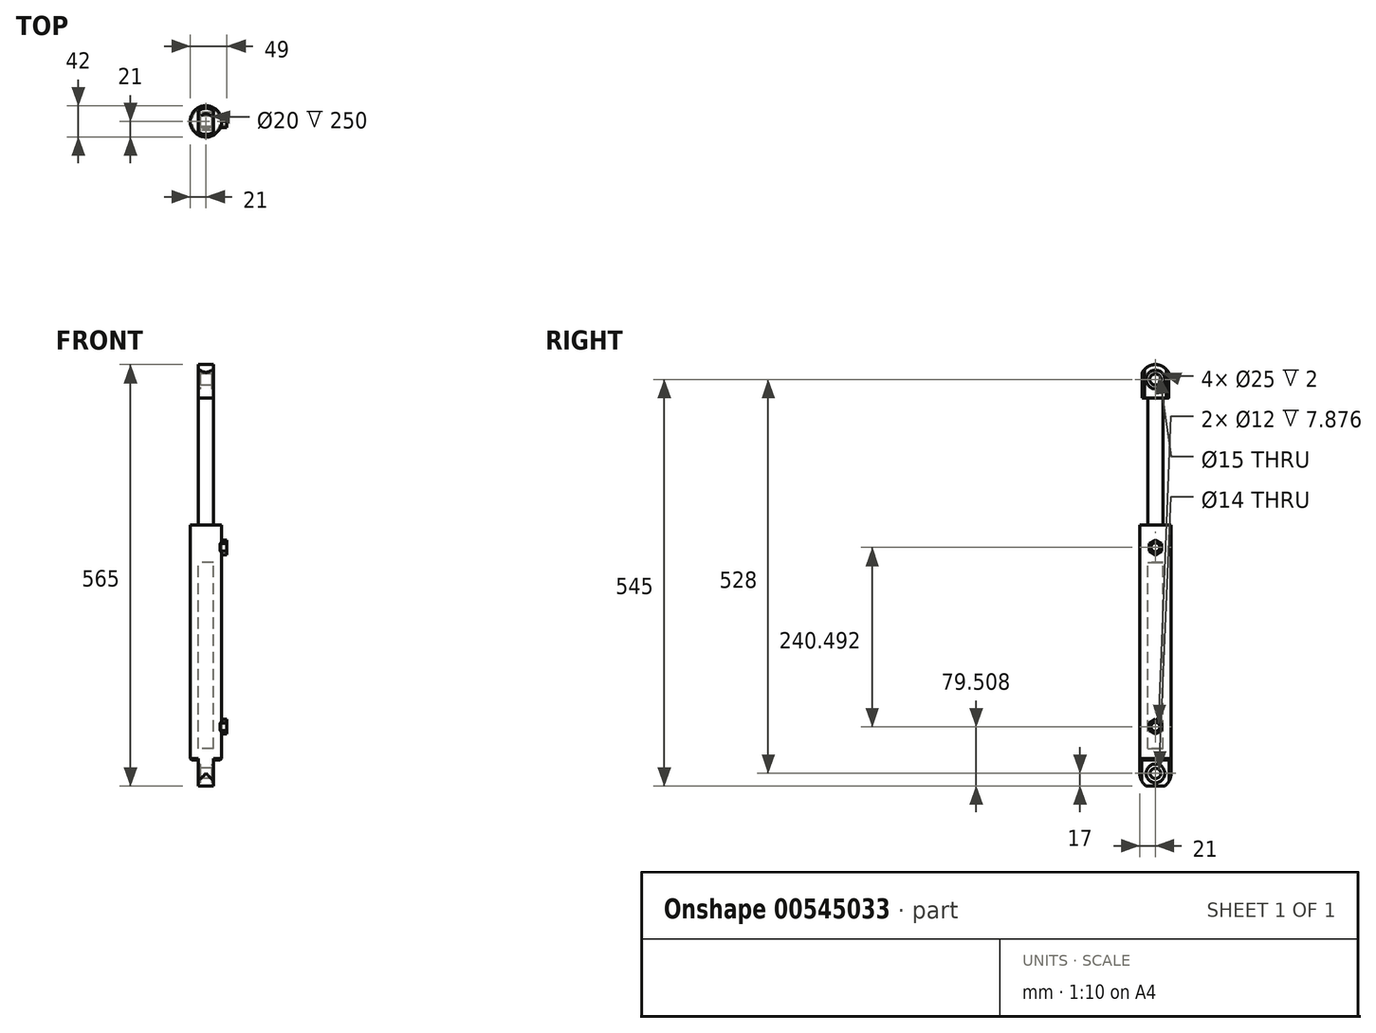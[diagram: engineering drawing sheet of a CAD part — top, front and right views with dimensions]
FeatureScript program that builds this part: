
annotation { "Feature Type Name" : "Feature", "Feature Type Description" : "" }
export const myFeature = defineFeature(function(context is Context, id is Id, definition is map)
    precondition{}
    {
        {
            var Q0;
            Q0=qCreatedBy(makeId("Top.planeOp"),FACE);
            var sketch = newSketch(context, id + "F0", { "sketchPlane" : qUnion([Q0])});
            skCircle(sketch, "E0", {"center": v(0, 0) * mm, "radius": 21 * mm});
            skSolve(sketch);
        }
        {
            var Q0;
            Q0 = qSketchRegion(id + "F0", true);
            extrude(context, id + "F1", {"entities" : qUnion([Q0]), "depth" : 315 * mm, "offsetDistance" : 25 * mm});
        }
        {
            var Q0;
            Q0=makeQuery(id+"F1.opExtrude","CAP_FACE",FACE,{"disambiguationData":[OSD([sQuery(id+"F0.wireOp",EDGE,"E0")])],"isStart":false});
            var sketch = newSketch(context, id + "F2", { "sketchPlane" : qUnion([Q0])});
            skCircle(sketch, "E1", {"center": v(0, 0) * mm, "radius": 10 * mm});
            skSolve(sketch);
        }
        {
            var Q0;
            Q0=makeQuery(id+"F2.imprint","IMPRINT",FACE,{"disambiguationData":[TD([[makeQuery(id+"F2.imprint","IMPRINT",EDGE,{"derivedFrom":sQuery(id+"F2.wireOp",EDGE,"E1")}),1.0]])]});
            extrude(context, id + "F3", {"entities" : qUnion([Q0]), "operationType" : NewBodyOperationType.REMOVE, "oppositeDirection" : true, "depth" : 300 * mm, "offsetDistance" : 25 * mm});
        }
        {
            var Q0;
            Q0=makeQuery(id+"F0.imprint","IMPRINT",FACE,{"disambiguationData":[TD([[makeQuery(id+"F0.imprint","IMPRINT",EDGE,{"derivedFrom":sQuery(id+"F0.wireOp",EDGE,"E0")}),1.0]])]});
            var sketch = newSketch(context, id + "F4", { "sketchPlane" : qUnion([Q0])});
            skCircle(sketch, "E2", {"center": v(0, 0) * mm, "radius": 21 * mm});
            skSolve(sketch);
        }
        {
            var Q0;
            Q0 = qSketchRegion(id + "F4", true);
            extrude(context, id + "F5", {"entities" : qUnion([Q0]), "operationType" : NewBodyOperationType.ADD, "oppositeDirection" : true, "depth" : 35 * mm, "offsetDistance" : 25 * mm});
        }
        {
            var Q0;
            Q0=makeQuery(id+"F5.opExtrude","CAP_FACE",FACE,{"disambiguationData":[OSD([sQuery(id+"F4.wireOp",EDGE,"E2")])],"isStart":false});
            var sketch = newSketch(context, id + "F6", { "sketchPlane" : qUnion([Q0])});
            skLineSegment(sketch, "E3", {"start": v(0, 0) * mm, "end": v(0, 21) * mm});
            skLineSegment(sketch, "E4.bottom", {"start": v(10, 24.47) * mm, "end": v(25.68, 24.47) * mm});
            skLineSegment(sketch, "E4.top", {"start": v(10, -25.36) * mm, "end": v(25.68, -25.36) * mm});
            skLineSegment(sketch, "E4.left", {"start": v(10, 24.47) * mm, "end": v(10, -25.36) * mm});
            skLineSegment(sketch, "E4.right", {"start": v(25.68, 24.47) * mm, "end": v(25.68, -25.36) * mm});
            skLineSegment(sketch, "E5.bottom", {"start": v(-10, 23.89) * mm, "end": v(-26.25, 23.89) * mm});
            skLineSegment(sketch, "E5.top", {"start": v(-10, -20.96) * mm, "end": v(-26.25, -20.96) * mm});
            skLineSegment(sketch, "E5.left", {"start": v(-10, 23.89) * mm, "end": v(-10, -20.96) * mm});
            skLineSegment(sketch, "E5.right", {"start": v(-26.25, 23.89) * mm, "end": v(-26.25, -20.96) * mm});
            skSolve(sketch);
        }
        {
            var Q0;
            Q0 = qSketchRegion(id + "F6", true);
            extrude(context, id + "F7", {"entities" : qUnion([Q0]), "operationType" : NewBodyOperationType.REMOVE, "oppositeDirection" : true, "depth" : 35 * mm, "offsetDistance" : 25 * mm});
        }
        {
            var Q0;
            Q0=makeQuery(id+"F7.boolean.opBoolean","COPY",FACE,{"derivedFrom":makeQuery(id+"F7.opExtrude","SWEPT_FACE",FACE,{"disambiguationData":[OSD([sQuery(id+"F6.wireOp",EDGE,"E5.left")])]})});
            var sketch = newSketch(context, id + "F8", { "sketchPlane" : qUnion([Q0])});
            skCircle(sketch, "E6", {"center": v(0, -18) * mm, "radius": 12.5 * mm});
            skSolve(sketch);
        }
        {
            var Q0;
            Q0 = qSketchRegion(id + "F8", true);
            extrude(context, id + "F9", {"entities" : qUnion([Q0]), "operationType" : NewBodyOperationType.REMOVE, "oppositeDirection" : true, "depth" : 2 * mm, "offsetDistance" : 25 * mm});
        }
        {
            var Q0;
            Q0=makeQuery(id+"F9.boolean.opBoolean","COPY",FACE,{"derivedFrom":makeQuery(id+"F9.opExtrude","CAP_FACE",FACE,{"disambiguationData":[OSD([sQuery(id+"F8.wireOp",EDGE,"E6")])],"isStart":false})});
            var sketch = newSketch(context, id + "F10", { "sketchPlane" : qUnion([Q0])});
            skCircle(sketch, "E7", {"center": v(0, -18) * mm, "radius": 7 * mm});
            skSolve(sketch);
        }
        {
            var Q0;
            Q0 = qSketchRegion(id + "F10", true);
            extrude(context, id + "F11", {"entities" : qUnion([Q0]), "operationType" : NewBodyOperationType.REMOVE, "oppositeDirection" : true, "depth" : 25 * mm, "offsetDistance" : 25 * mm});
        }
        {
            var Q0;
            Q0=makeQuery(id+"F7.boolean.opBoolean","COPY",FACE,{"derivedFrom":makeQuery(id+"F7.opExtrude","SWEPT_FACE",FACE,{"disambiguationData":[OSD([sQuery(id+"F6.wireOp",EDGE,"E4.left")])]})});
            var sketch = newSketch(context, id + "F12", { "sketchPlane" : qUnion([Q0])});
            skCircle(sketch, "E8", {"center": v(0, -18) * mm, "radius": 12.5 * mm});
            skSolve(sketch);
        }
        {
            var Q0;
            Q0 = qSketchRegion(id + "F12", true);
            extrude(context, id + "F13", {"entities" : qUnion([Q0]), "operationType" : NewBodyOperationType.REMOVE, "oppositeDirection" : true, "depth" : 2 * mm, "offsetDistance" : 25 * mm});
        }
        {
            var Q0;
            Q0=makeQuery(id+"F7.boolean.opBoolean","COPY",FACE,{"derivedFrom":makeQuery(id+"F7.opExtrude","SWEPT_FACE",FACE,{"disambiguationData":[OSD([sQuery(id+"F6.wireOp",EDGE,"E5.left")])]})});
            var sketch = newSketch(context, id + "F14", { "sketchPlane" : qUnion([Q0])});
            skArc(sketch, "E9", {"start": v(-21, -18) * mm, "mid": v(0, -39) * mm, "end": v(21, -18) * mm});
            skArc(sketch, "E10", {"start": v(-30, -18) * mm, "mid": v(0, -48) * mm, "end": v(30, -18) * mm});
            skLineSegment(sketch, "E11", {"start": v(30, -18) * mm, "end": v(21, -18) * mm});
            skLineSegment(sketch, "E12.trimOffspring", {"start": v(-21, -18) * mm, "end": v(-30, -18) * mm});
            skSolve(sketch);
        }
        {
            var Q0;
            Q0 = qSketchRegion(id + "F14", true);
            extrude(context, id + "F15", {"entities" : qUnion([Q0]), "operationType" : NewBodyOperationType.REMOVE, "oppositeDirection" : true, "depth" : 25 * mm, "offsetDistance" : 25 * mm});
        }
        {
            var Q0;
            Q0=makeQuery(id+"F7.boolean.opBoolean","INTERSECT",EDGE,{"derivedFrom":[makeQuery(id+"F5.boolean.opBoolean","MERGE",FACE,{"derivedFrom":[makeQuery(id+"F1.opExtrude","SWEPT_FACE",FACE,{"disambiguationData":[OSD([sQuery(id+"F0.wireOp",EDGE,"E0")])]}),makeQuery(id+"F5.opExtrude","SWEPT_FACE",FACE,{"disambiguationData":[OSD([sQuery(id+"F4.wireOp",EDGE,"E2")])]})]}),makeQuery(id+"F7.opExtrude","CAP_FACE",FACE,{"disambiguationData":[OSD([sQuery(id+"F6.wireOp",EDGE,"E4.bottom"),sQuery(id+"F6.wireOp",EDGE,"E4.top"),sQuery(id+"F6.wireOp",EDGE,"E4.left"),sQuery(id+"F6.wireOp",EDGE,"E4.right")])],"isStart":false})]});
            var Q1;
            Q1=makeQuery(id+"F7.boolean.opBoolean","INTERSECT",EDGE,{"derivedFrom":[makeQuery(id+"F5.boolean.opBoolean","MERGE",FACE,{"derivedFrom":[makeQuery(id+"F1.opExtrude","SWEPT_FACE",FACE,{"disambiguationData":[OSD([sQuery(id+"F0.wireOp",EDGE,"E0")])]}),makeQuery(id+"F5.opExtrude","SWEPT_FACE",FACE,{"disambiguationData":[OSD([sQuery(id+"F4.wireOp",EDGE,"E2")])]})]}),makeQuery(id+"F7.opExtrude","CAP_FACE",FACE,{"disambiguationData":[OSD([sQuery(id+"F6.wireOp",EDGE,"E5.bottom"),sQuery(id+"F6.wireOp",EDGE,"E5.top"),sQuery(id+"F6.wireOp",EDGE,"E5.left"),sQuery(id+"F6.wireOp",EDGE,"E5.right")])],"isStart":false})]});
            chamfer(context, id + "F16", {"entities" : qUnion([Q0, Q1]), "width" : 2 * mm, "tangentPropagation" : true});
        }
        {
            var Q0;
            Q0=makeQuery(id+"F1.opExtrude","CAP_FACE",FACE,{"disambiguationData":[OSD([sQuery(id+"F0.wireOp",EDGE,"E0")])],"isStart":false});
            var sketch = newSketch(context, id + "F17", { "sketchPlane" : qUnion([Q0])});
            skCircle(sketch, "E13", {"center": v(0, 0) * mm, "radius": 10 * mm});
            skSolve(sketch);
        }
        {
            var Q0;
            Q0=makeQuery(id+"F17.imprint","IMPRINT",FACE,{"disambiguationData":[TD([[makeQuery(id+"F17.imprint","IMPRINT",EDGE,{"derivedFrom":sQuery(id+"F17.wireOp",EDGE,"E13")}),1.0]])]});
            extrude(context, id + "F18", {"entities" : qUnion([Q0]), "depth" : 200 * mm, "offsetDistance" : 25 * mm});
        }
        {
            var Q0;
            Q0=makeQuery(id+"F18.opExtrude","CAP_FACE",FACE,{"disambiguationData":[OSD([sQuery(id+"F17.wireOp",EDGE,"E13")])],"isStart":true});
            var sketch = newSketch(context, id + "F19", { "sketchPlane" : qUnion([Q0])});
            skCircle(sketch, "E14", {"center": v(0, 0) * mm, "radius": 10 * mm});
            skSolve(sketch);
        }
        {
            var Q0;
            Q0=makeQuery(id+"F19.imprint","IMPRINT",FACE,{"disambiguationData":[TD([[makeQuery(id+"F19.imprint","IMPRINT",EDGE,{"derivedFrom":sQuery(id+"F19.wireOp",EDGE,"E14")}),-1.0]])]});
            var Q1;
            Q1 = qSketchRegion(id + "F19", true);
            extrude(context, id + "F20", {"entities" : qUnion([Q0, Q1]), "operationType" : NewBodyOperationType.ADD, "depth" : 50 * mm, "offsetDistance" : 25 * mm});
        }
        {
            var Q0;
            Q0=makeQuery(id+"F18.opExtrude","CAP_FACE",FACE,{"disambiguationData":[OSD([sQuery(id+"F17.wireOp",EDGE,"E13")])],"isStart":false});
            var sketch = newSketch(context, id + "F21", { "sketchPlane" : qUnion([Q0])});
            skCircle(sketch, "E15", {"center": v(0, 0) * mm, "radius": 17.5 * mm});
            skSolve(sketch);
        }
        {
            var Q0;
            Q0=makeQuery(id+"F21.imprint","IMPRINT",FACE,{"disambiguationData":[TD([[makeQuery(id+"F21.imprint","IMPRINT",EDGE,{"derivedFrom":sQuery(id+"F21.wireOp",EDGE,"E15")}),1.0]])]});
            var Q1;
            Q1=makeQuery(id+"F21.imprint","IMPRINT",FACE,{"disambiguationData":[TD([[makeQuery(id+"F21.imprint","IMPRINT",EDGE,{"derivedFrom":makeQuery(id+"F18.opExtrude","CAP_EDGE",EDGE,{"disambiguationData":[OSD([sQuery(id+"F17.wireOp",EDGE,"E13")])],"isStart":false})}),1.0]])]});
            extrude(context, id + "F22", {"entities" : qUnion([Q0, Q1]), "operationType" : NewBodyOperationType.ADD, "oppositeDirection" : true, "depth" : 30 * mm, "offsetDistance" : 25 * mm});
        }
        {
            var Q0;
            Q0=makeQuery(id+"F22.boolean.opBoolean","MERGE",FACE,{"derivedFrom":[makeQuery(id+"F18.opExtrude","CAP_FACE",FACE,{"disambiguationData":[OSD([sQuery(id+"F17.wireOp",EDGE,"E13")])],"isStart":false}),makeQuery(id+"F22.opExtrude","CAP_FACE",FACE,{"disambiguationData":[OSD([sQuery(id+"F21.wireOp",EDGE,"E15")])],"isStart":true})]});
            var sketch = newSketch(context, id + "F23", { "sketchPlane" : qUnion([Q0])});
            skSolve(sketch);
        }
        {
            var Q0;
            Q0=makeQuery(id+"F23.imprint","IMPRINT",FACE,{"disambiguationData":[TD([[makeQuery(id+"F23.imprint","IMPRINT",EDGE,{"derivedFrom":makeQuery(id+"F22.opExtrude","CAP_EDGE",EDGE,{"disambiguationData":[OSD([sQuery(id+"F21.wireOp",EDGE,"E15")])],"isStart":true})}),1.0]])]});
            extrude(context, id + "F24", {"entities" : qUnion([Q0]), "operationType" : NewBodyOperationType.ADD, "depth" : 20 * mm, "offsetDistance" : 25 * mm});
        }
        {
            var Q0;
            Q0=makeQuery(id+"F24.opExtrude","CAP_FACE",FACE,{"disambiguationData":[OSD([sQuery(id+"F21.wireOp",EDGE,"E15")])],"isStart":false});
            var sketch = newSketch(context, id + "F25", { "sketchPlane" : qUnion([Q0])});
            skLineSegment(sketch, "E16", {"start": v(0, 0) * mm, "end": v(0, 17.5) * mm});
            skLineSegment(sketch, "E17.bottom", {"start": v(10, 21.05) * mm, "end": v(24.1, 21.05) * mm});
            skLineSegment(sketch, "E17.top", {"start": v(10, -21.98) * mm, "end": v(24.1, -21.98) * mm});
            skLineSegment(sketch, "E17.left", {"start": v(10, 21.05) * mm, "end": v(10, -21.98) * mm});
            skLineSegment(sketch, "E17.right", {"start": v(24.1, 21.05) * mm, "end": v(24.1, -21.98) * mm});
            skLineSegment(sketch, "E18.bottom", {"start": v(-10, 20.84) * mm, "end": v(-21.86, 20.84) * mm});
            skLineSegment(sketch, "E18.top", {"start": v(-10, -21.1) * mm, "end": v(-21.86, -21.1) * mm});
            skLineSegment(sketch, "E18.left", {"start": v(-10, 20.84) * mm, "end": v(-10, -21.1) * mm});
            skLineSegment(sketch, "E18.right", {"start": v(-21.86, 20.84) * mm, "end": v(-21.86, -21.1) * mm});
            skSolve(sketch);
        }
        {
            var Q0;
            {var subQ0=sQuery(id+"F25.wireOp",EDGE,"E18.left");var subQ1=makeQuery(id+"F24.opExtrude","CAP_EDGE",EDGE,{"disambiguationData":[OSD([sQuery(id+"F21.wireOp",EDGE,"E15")])],"isStart":false});var subQ2=makeQuery(id+"F25.imprint","INTERSECT",VERTEX,{"disambiguationData":[OD(0.0)],"derivedFrom":[subQ1,subQ0]});Q0=makeQuery(id+"F25.imprint","IMPRINT",FACE,{"disambiguationData":[TD([[makeQuery(id+"F25.imprint","IMPRINT",EDGE,{"disambiguationData":[TD([[subQ2,-1.0]])],"derivedFrom":subQ0}),-1.0]])]});}
            var Q1;
            {var subQ0=sQuery(id+"F25.wireOp",EDGE,"E17.left");var subQ1=makeQuery(id+"F24.opExtrude","CAP_EDGE",EDGE,{"disambiguationData":[OSD([sQuery(id+"F21.wireOp",EDGE,"E15")])],"isStart":false});var subQ2=makeQuery(id+"F25.imprint","INTERSECT",VERTEX,{"disambiguationData":[OD(0.0)],"derivedFrom":[subQ1,subQ0]});Q1=makeQuery(id+"F25.imprint","IMPRINT",FACE,{"disambiguationData":[TD([[makeQuery(id+"F25.imprint","IMPRINT",EDGE,{"disambiguationData":[TD([[subQ2,-1.0]])],"derivedFrom":subQ0}),1.0]])]});}
            extrude(context, id + "F26", {"entities" : qUnion([Q0, Q1]), "operationType" : NewBodyOperationType.REMOVE, "oppositeDirection" : true, "depth" : 60 * mm, "offsetDistance" : 25 * mm});
        }
        {
            var Q0;
            Q0=makeQuery(id+"F26.boolean.opBoolean","COPY",FACE,{"derivedFrom":makeQuery(id+"F26.opExtrude","SWEPT_FACE",FACE,{"disambiguationData":[OSD([sQuery(id+"F25.wireOp",EDGE,"E18.left")])]})});
            var sketch = newSketch(context, id + "F27", { "sketchPlane" : qUnion([Q0])});
            skLineSegment(sketch, "E19", {"start": v(0, 535) * mm, "end": v(0, 485) * mm});
            skCircle(sketch, "E20", {"center": v(0, 510) * mm, "radius": 12.5 * mm});
            skSolve(sketch);
        }
        {
            var Q0;
            Q0 = qSketchRegion(id + "F27", true);
            extrude(context, id + "F28", {"entities" : qUnion([Q0]), "operationType" : NewBodyOperationType.REMOVE, "oppositeDirection" : true, "depth" : 2 * mm, "offsetDistance" : 25 * mm});
        }
        {
            var Q0;
            Q0=makeQuery(id+"F28.boolean.opBoolean","COPY",FACE,{"derivedFrom":makeQuery(id+"F28.opExtrude","CAP_FACE",FACE,{"disambiguationData":[OSD([sQuery(id+"F27.wireOp",EDGE,"E20")])],"isStart":false})});
            var sketch = newSketch(context, id + "F29", { "sketchPlane" : qUnion([Q0])});
            skCircle(sketch, "E21", {"center": v(0, 510) * mm, "radius": 7.5 * mm});
            skSolve(sketch);
        }
        {
            var Q0;
            Q0=makeQuery(id+"F29.imprint","IMPRINT",FACE,{"disambiguationData":[TD([[makeQuery(id+"F29.imprint","IMPRINT",EDGE,{"derivedFrom":sQuery(id+"F29.wireOp",EDGE,"E21")}),1.0]])]});
            var Q1;
            Q1 = qSketchRegion(id + "F29", true);
            extrude(context, id + "F30", {"entities" : qUnion([Q0, Q1]), "operationType" : NewBodyOperationType.REMOVE, "oppositeDirection" : true, "depth" : 25 * mm, "offsetDistance" : 25 * mm});
        }
        {
            var Q0;
            Q0=makeQuery(id+"F26.boolean.opBoolean","COPY",FACE,{"derivedFrom":makeQuery(id+"F26.opExtrude","SWEPT_FACE",FACE,{"disambiguationData":[OSD([sQuery(id+"F25.wireOp",EDGE,"E17.left")])]})});
            var sketch = newSketch(context, id + "F31", { "sketchPlane" : qUnion([Q0])});
            skCircle(sketch, "E22", {"center": v(0, 510) * mm, "radius": 12.5 * mm});
            skSolve(sketch);
        }
        {
            var Q0;
            Q0 = qSketchRegion(id + "F31", true);
            var Q1;
            Q1=makeQuery(id+"F31.imprint","IMPRINT",FACE,{"disambiguationData":[TD([[makeQuery(id+"F31.imprint","IMPRINT",EDGE,{"derivedFrom":sQuery(id+"F31.wireOp",EDGE,"E22")}),1.0]])]});
            extrude(context, id + "F32", {"entities" : qUnion([Q0, Q1]), "operationType" : NewBodyOperationType.REMOVE, "oppositeDirection" : true, "depth" : 2 * mm, "offsetDistance" : 25 * mm});
        }
        {
            var Q0;
            Q0=makeQuery(id+"F26.boolean.opBoolean","COPY",FACE,{"derivedFrom":makeQuery(id+"F26.opExtrude","SWEPT_FACE",FACE,{"disambiguationData":[OSD([sQuery(id+"F25.wireOp",EDGE,"E18.left")])]})});
            var sketch = newSketch(context, id + "F33", { "sketchPlane" : qUnion([Q0])});
            skArc(sketch, "E23", {"start": v(20, 510) * mm, "mid": v(0, 530) * mm, "end": v(-20, 510) * mm});
            skArc(sketch, "E24", {"start": v(33.98, 510) * mm, "mid": v(0, 543.98) * mm, "end": v(-33.98, 510) * mm});
            skLineSegment(sketch, "E25", {"start": v(20, 510) * mm, "end": v(33.98, 510) * mm});
            skPoint(sketch, "E25.endSnap0", {"position": v(14.36, 510) * mm});
            skLineSegment(sketch, "E26", {"start": v(33.98, 510) * mm, "end": v(20, 510) * mm});
            skLineSegment(sketch, "E27.trimOffspring", {"start": v(-20, 510) * mm, "end": v(-33.98, 510) * mm});
            skSolve(sketch);
        }
        {
            var Q0;
            Q0 = qSketchRegion(id + "F33", true);
            extrude(context, id + "F34", {"entities" : qUnion([Q0]), "operationType" : NewBodyOperationType.REMOVE, "oppositeDirection" : true, "depth" : 25 * mm, "offsetDistance" : 25 * mm});
        }
        {
            var Q0;
            Q0=makeQuery(id+"F7.boolean.opBoolean","COPY",FACE,{"derivedFrom":makeQuery(id+"F7.opExtrude","SWEPT_FACE",FACE,{"disambiguationData":[OSD([sQuery(id+"F6.wireOp",EDGE,"E4.left")])]})});
            var sketch = newSketch(context, id + "F35", { "sketchPlane" : qUnion([Q0])});
            skPoint(sketch, "E28.endSnap0", {"position": v(0, -35) * mm});
            skArc(sketch, "E29.cCircle", {"start": v(0.24, 36.01) * mm, "mid": v(-0.2, 53) * mm, "end": v(0.17, 36) * mm, "construction": true});
            skLineSegment(sketch, "E29.0", {"start": v(0, 54.32) * mm, "end": v(8.5, 49.42) * mm});
            skLineSegment(sketch, "E29.1", {"start": v(8.5, 49.42) * mm, "end": v(8.5, 39.6) * mm});
            skLineSegment(sketch, "E29.2", {"start": v(8.5, 39.6) * mm, "end": v(0, 34.7) * mm});
            skLineSegment(sketch, "E29.3", {"start": v(0, 34.7) * mm, "end": v(-8.5, 39.6) * mm});
            skLineSegment(sketch, "E29.4", {"start": v(-8.5, 39.6) * mm, "end": v(-8.5, 49.42) * mm});
            skLineSegment(sketch, "E29.5", {"start": v(-8.5, 49.42) * mm, "end": v(0, 54.32) * mm});
            skPoint(sketch, "E29.0.midPoint", {"position": v(4.25, 51.87) * mm});
            skCircle(sketch, "E30.cCircle", {"center": v(0, 285) * mm, "radius": 8.5 * mm, "construction": true});
            skLineSegment(sketch, "E30.0", {"start": v(8.5, 289.9) * mm, "end": v(8.5, 280.1) * mm});
            skLineSegment(sketch, "E30.1", {"start": v(8.5, 280.1) * mm, "end": v(0, 275.19) * mm});
            skLineSegment(sketch, "E30.2", {"start": v(0, 275.19) * mm, "end": v(-8.5, 280.1) * mm});
            skLineSegment(sketch, "E30.3", {"start": v(-8.5, 280.1) * mm, "end": v(-8.5, 289.9) * mm});
            skLineSegment(sketch, "E30.4", {"start": v(-8.5, 289.9) * mm, "end": v(0, 294.81) * mm});
            skLineSegment(sketch, "E30.5", {"start": v(0, 294.81) * mm, "end": v(8.5, 289.9) * mm});
            skPoint(sketch, "E30.0.midPoint", {"position": v(8.5, 285) * mm});
            skCircle(sketch, "E31", {"center": v(0, 285) * mm, "radius": 6 * mm});
            skCircle(sketch, "E32", {"center": v(0, 44.5) * mm, "radius": 6 * mm});
            skLineSegment(sketch, "E33.trimOffspring", {"start": v(0.17, 36) * mm, "end": v(0.19, 34.8) * mm});
            skPoint(sketch, "E34.end.orphan", {"position": v(0, 0) * mm});
            skPoint(sketch, "E34.start.orphan", {"position": v(0, -30.5) * mm});
            skLineSegment(sketch, "E35", {"start": v(0, 0) * mm, "end": v(0, 314.97) * mm});
            skLineSegment(sketch, "E36", {"start": v(-21, -18) * mm, "end": v(-21, 315) * mm});
            skLineSegment(sketch, "E37", {"start": v(21, 315) * mm, "end": v(21, -18) * mm});
            skLineSegment(sketch, "E38.0", {"start": v(-21, 315) * mm, "end": v(21, 315) * mm});
            skSolve(sketch);
        }
        {
            var Q0;
            Q0 = qSketchRegion(id + "F35", true);
            extrude(context, id + "F36", {"entities" : qUnion([Q0]), "operationType" : NewBodyOperationType.ADD, "depth" : 18 * mm, "offsetDistance" : 25 * mm});
        }
    });
